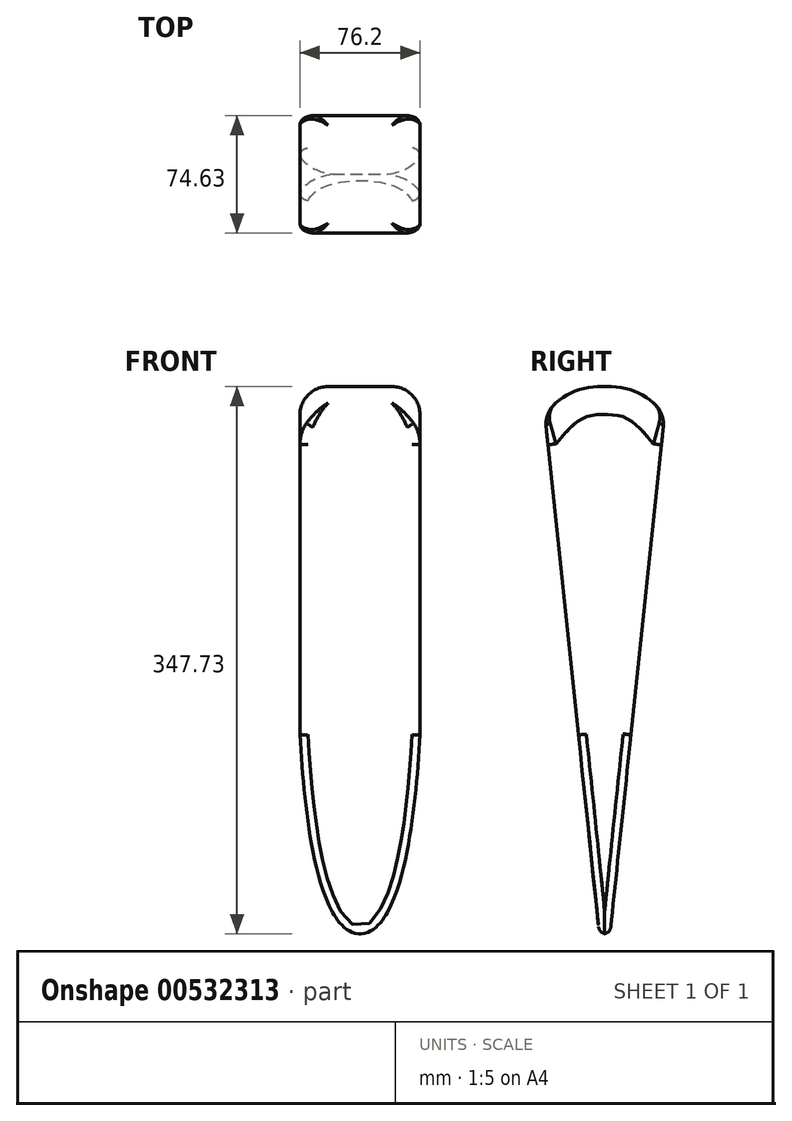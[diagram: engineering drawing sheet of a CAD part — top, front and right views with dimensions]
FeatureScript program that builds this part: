
annotation { "Feature Type Name" : "Feature", "Feature Type Description" : "" }
export const myFeature = defineFeature(function(context is Context, id is Id, definition is map)
    precondition{}
    {
        {
            var Q0;
            Q0=qCreatedBy(makeId("Right.planeOp"),FACE);
            var sketch = newSketch(context, id + "F0", { "sketchPlane" : qUnion([Q0])});
            skLineSegment(sketch, "E0", {"start": v(-41.5, 19.95) * mm, "end": v(-6.79, -310.25) * mm});
            skLineSegment(sketch, "E1", {"start": v(34.7, 19.95) * mm, "end": v(0, -310.25) * mm});
            skLineSegment(sketch, "E2", {"start": v(-41.5, 19.95) * mm, "end": v(34.7, 19.95) * mm, "construction": true});
            skPoint(sketch, "E3", {"position": v(-3.4, 37.48) * mm});
            skFitSpline(sketch, "E4", {"points": [v(-41.5, 19.95) * mm, v(-3.4, 37.48) * mm, v(34.7, 19.95) * mm], "startDerivative": vector(83.82, 96.01) * mm, "endDerivative": vector(83.82, -96.01) * mm});
            skLineSegment(sketch, "E5", {"start": v(-41.5, 19.95) * mm, "end": v(-3.4, 37.48) * mm, "construction": true});
            skLineSegment(sketch, "E6", {"start": v(34.7, 19.95) * mm, "end": v(-3.4, 37.48) * mm, "construction": true});
            skLineSegment(sketch, "E7", {"start": v(-3.4, 37.48) * mm, "end": v(-3.4, 19.95) * mm, "construction": true});
            skLineSegment(sketch, "E8", {"start": v(-27.52, 35.95) * mm, "end": v(20.74, 35.95) * mm, "construction": true});
            skLineSegment(sketch, "E9", {"start": v(-41.5, 19.95) * mm, "end": v(-27.52, 35.95) * mm, "construction": true});
            skLineSegment(sketch, "E10", {"start": v(20.74, 35.95) * mm, "end": v(34.7, 19.95) * mm, "construction": true});
            skLineSegment(sketch, "E11", {"start": v(0, -310.25) * mm, "end": v(-6.79, -310.25) * mm});
            skSolve(sketch);
        }
        {
            var Q0;
            Q0=qCreatedBy(makeId("Front.planeOp"),FACE);
            var sketch = newSketch(context, id + "F1", { "sketchPlane" : qUnion([Q0])});
            skLineSegment(sketch, "E12", {"start": v(-235.99, 30.47) * mm, "end": v(-235.99, -96.53) * mm, "construction": true});
            skLineSegment(sketch, "E13", {"start": v(-235.99, -96.53) * mm, "end": v(-312.19, -96.53) * mm, "construction": true});
            skLineSegment(sketch, "E14", {"start": v(-312.19, -96.53) * mm, "end": v(-312.19, 30.47) * mm, "construction": true});
            skLineSegment(sketch, "E15", {"start": v(-274.09, -96.53) * mm, "end": v(-274.09, -165.83) * mm, "construction": true});
            skFitSpline(sketch, "E16", {"points": [v(-312.19, 30.47) * mm, v(-274.09, -96.53) * mm, v(-235.99, 30.47) * mm], "startDerivative": vector(30.48, -579.12) * mm, "endDerivative": vector(30.48, 579.12) * mm});
            skLineSegment(sketch, "E17", {"start": v(-312.19, -96.53) * mm, "end": v(-307.1, -66.05) * mm, "construction": true});
            skLineSegment(sketch, "E18", {"start": v(-235.99, -96.53) * mm, "end": v(-241.07, -66.05) * mm, "construction": true});
            skLineSegment(sketch, "E19", {"start": v(-312.19, 30.47) * mm, "end": v(-307.1, -66.05) * mm, "construction": true});
            skLineSegment(sketch, "E20", {"start": v(-235.99, 30.47) * mm, "end": v(-241.07, -66.05) * mm, "construction": true});
            skLineSegment(sketch, "E21.top", {"start": v(-370.45, -109.47) * mm, "end": v(-169.48, -109.47) * mm});
            skLineSegment(sketch, "E21.left", {"start": v(-370.45, 30.47) * mm, "end": v(-370.45, -109.47) * mm});
            skLineSegment(sketch, "E21.right", {"start": v(-169.48, 30.47) * mm, "end": v(-169.48, -109.47) * mm});
            skLineSegment(sketch, "E22", {"start": v(-312.19, 30.47) * mm, "end": v(-370.45, 30.47) * mm});
            skLineSegment(sketch, "E23", {"start": v(-235.99, 30.47) * mm, "end": v(-169.48, 30.47) * mm});
            skSolve(sketch);
        }
        {
            var Q0;
            Q0=qCreatedBy(makeId("Right.planeOp"),FACE);
            cPlane(context, id + "F2", {"entities" : qUnion([Q0]), "cplaneType" : CPlaneType.OFFSET, "offset" : 38.1 * mm, "width" : 152.4 * mm, "height" : 152.4 * mm});
        }
        {
            var Q0;
            Q0=makeQuery(id+"F0.imprint","IMPRINT",FACE,{"disambiguationData":[TD([[makeQuery(id+"F0.imprint","IMPRINT",EDGE,{"derivedFrom":sQuery(id+"F0.wireOp",EDGE,"E0")}),1.0]])]});
            extrude(context, id + "F3", {"entities" : qUnion([Q0]), "depth" : 76.2 * mm, "symmetric" : true});
        }
        {
            var Q0;
            Q0=qSketchRegion(id+"F1",true);
            extrude(context, id + "F4", {"entities" : qUnion([Q0]), "depth" : 101.6 * mm, "symmetric" : true});
        }
        {
            var Q0;
            Q0=qCreatedBy(id+"F2.planeOp",FACE);
            var sketch = newSketch(context, id + "F5", { "sketchPlane" : qUnion([Q0])});
            skLineSegment(sketch, "E24", {"start": v(-3.4, -310.25) * mm, "end": v(-3.4, -183.25) * mm, "construction": true});
            skSolve(sketch);
        }
        {
            var Q0;
            Q0=makeQuery(id+"F4.opExtrude","SWEPT_EDGE",EDGE,{"disambiguationData":[OSD([sQuery(id+"F1.wireOp",EDGE,"E16"),sQuery(id+"F1.wireOp",EDGE,"E23")])]});
            cPoint(context, id + "F6", {"entities" : qUnion([Q0]), "parameter" : 0.5});
        }
        {
            var Q0;
            Q0=makeQuery(id+"F4.opExtrude","SWEPT_BODY",BODY,{"disambiguationData":[OSD([sQuery(id+"F1.wireOp",EDGE,"E16"),sQuery(id+"F1.wireOp",EDGE,"E21.top"),sQuery(id+"F1.wireOp",EDGE,"E21.left"),sQuery(id+"F1.wireOp",EDGE,"E21.right"),sQuery(id+"F1.wireOp",EDGE,"E22"),sQuery(id+"F1.wireOp",EDGE,"E23")])]});
            var Q1;
            Q1=qCreatedBy(id+"F6",VERTEX);
            var Q2;
            Q2=sQuery(id+"F5.wireOp",VERTEX,"E24.end");
            transform(context, id + "F7", {"entities" : qUnion([Q0]), "transformType" : TransformType.TRANSLATION_ENTITY, "oppositeDirectionEntity" : false, "transformLine" : qUnion([Q1, Q2]), "makeCopy" : false});
        }
        {
            var Q0;
            Q0=makeQuery(id+"F4.opExtrude","SWEPT_BODY",BODY,{"disambiguationData":[OSD([sQuery(id+"F1.wireOp",EDGE,"E16"),sQuery(id+"F1.wireOp",EDGE,"E21.top"),sQuery(id+"F1.wireOp",EDGE,"E21.left"),sQuery(id+"F1.wireOp",EDGE,"E21.right"),sQuery(id+"F1.wireOp",EDGE,"E22"),sQuery(id+"F1.wireOp",EDGE,"E23")])]});
            var Q1;
            Q1=makeQuery(id+"F3.opExtrude","SWEPT_BODY",BODY,{"disambiguationData":[OSD([sQuery(id+"F0.wireOp",EDGE,"E0"),sQuery(id+"F0.wireOp",EDGE,"E1"),sQuery(id+"F0.wireOp",EDGE,"E4"),sQuery(id+"F0.wireOp",EDGE,"E11")])]});
            booleanBodies(context, id + "F8", {"operationType" : BooleanOperationType.SUBTRACTION, "tools" : qUnion([Q0]), "targets" : qUnion([Q1])});
        }
        {
            var Q0;
            Q0=makeQuery(id+"F8.opBoolean","INTERSECT",EDGE,{"derivedFrom":[makeQuery(id+"F3.opExtrude","SWEPT_FACE",FACE,{"disambiguationData":[OSD([sQuery(id+"F0.wireOp",EDGE,"E1")])]}),makeQuery(id+"F4.opExtrude","SWEPT_FACE",FACE,{"disambiguationData":[OSD([sQuery(id+"F1.wireOp",EDGE,"E16")])]})]});
            var Q1;
            Q1=makeQuery(id+"F8.opBoolean","INTERSECT",EDGE,{"derivedFrom":[makeQuery(id+"F3.opExtrude","SWEPT_FACE",FACE,{"disambiguationData":[OSD([sQuery(id+"F0.wireOp",EDGE,"E0")])]}),makeQuery(id+"F4.opExtrude","SWEPT_FACE",FACE,{"disambiguationData":[OSD([sQuery(id+"F1.wireOp",EDGE,"E16")])]})]});
            fillet(context, id + "F9", {"entities" : qUnion([Q0, Q1]), "radius" : 5.08 * mm, "tangentPropagation" : true, "allowEdgeOverflow" : false});
        }
        {
            var Q0;
            Q0=makeQuery(id+"F3.opExtrude","CAP_EDGE",EDGE,{"disambiguationData":[OSD([sQuery(id+"F0.wireOp",EDGE,"E0")])],"isStart":true});
            var Q1;
            Q1=makeQuery(id+"F3.opExtrude","CAP_EDGE",EDGE,{"disambiguationData":[OSD([sQuery(id+"F0.wireOp",EDGE,"E0")])],"isStart":false});
            var Q2;
            Q2=makeQuery(id+"F3.opExtrude","CAP_EDGE",EDGE,{"disambiguationData":[OSD([sQuery(id+"F0.wireOp",EDGE,"E1")])],"isStart":false});
            var Q3;
            Q3=makeQuery(id+"F3.opExtrude","CAP_EDGE",EDGE,{"disambiguationData":[OSD([sQuery(id+"F0.wireOp",EDGE,"E1")])],"isStart":true});
            fillet(context, id + "F10", {"entities" : qUnion([Q0, Q1, Q2, Q3]), "radius" : 5.08 * mm, "tangentPropagation" : true, "allowEdgeOverflow" : false});
        }
        {
            var Q0;
            Q0=makeQuery(id+"F3.opExtrude","SWEPT_FACE",FACE,{"disambiguationData":[OSD([sQuery(id+"F0.wireOp",EDGE,"E4")])]});
            fillet(context, id + "F11", {"entities" : qUnion([Q0]), "radius" : 17.78 * mm, "tangentPropagation" : true, "allowEdgeOverflow" : false});
        }
    });
